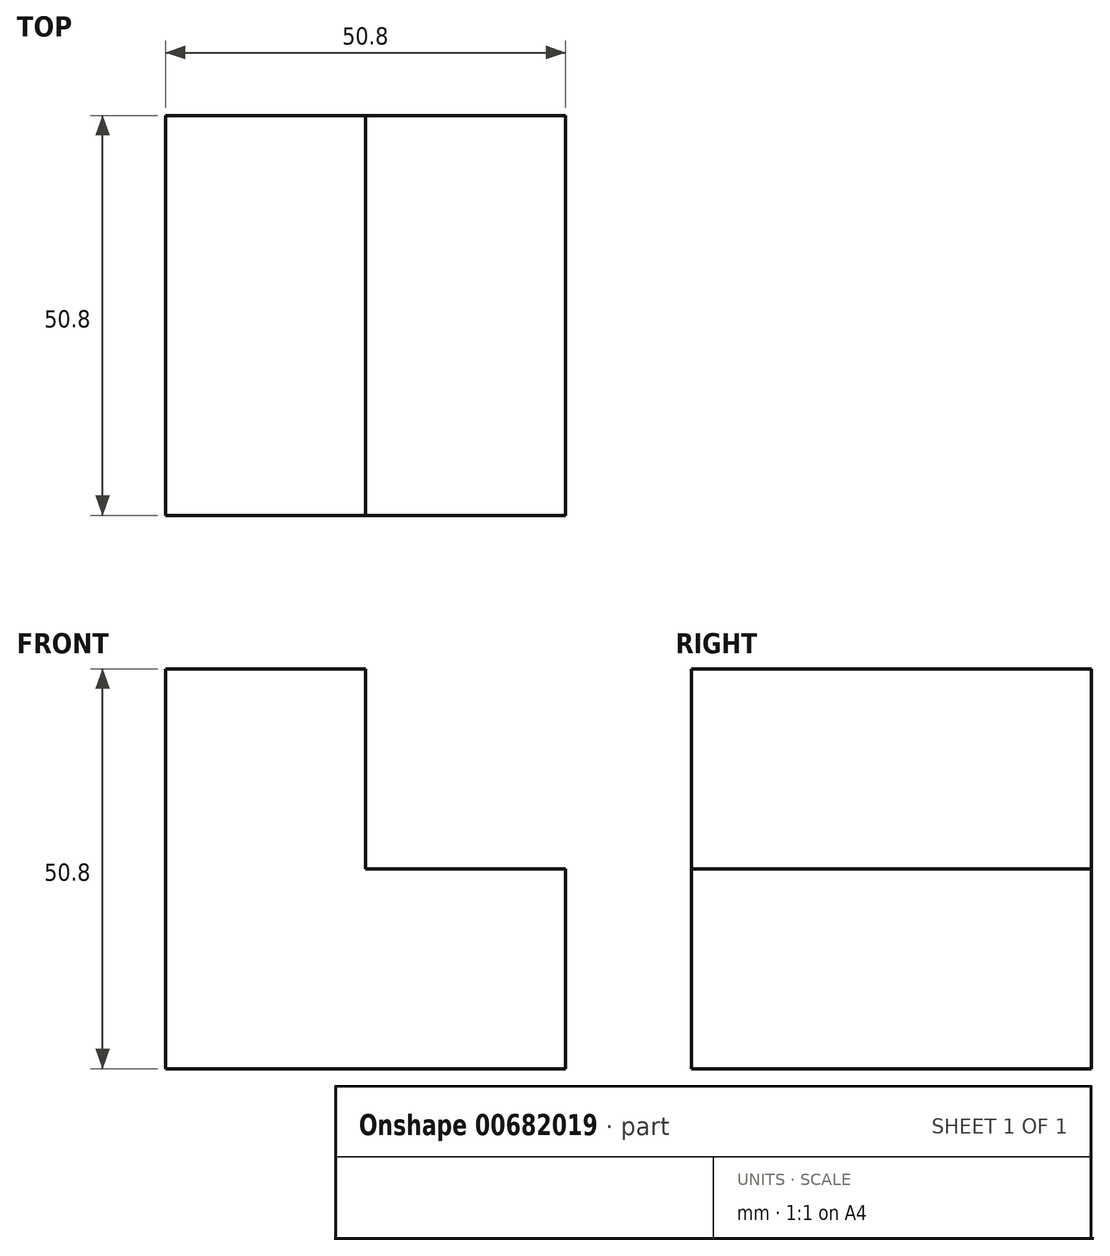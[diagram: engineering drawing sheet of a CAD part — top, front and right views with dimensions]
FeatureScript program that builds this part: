
annotation { "Feature Type Name" : "Feature", "Feature Type Description" : "" }
export const myFeature = defineFeature(function(context is Context, id is Id, definition is map)
    precondition{}
    {
        {
            var Q0;
            Q0=qCreatedBy(makeId("Front.planeOp"),FACE);
            var sketch = newSketch(context, id + "F0", { "sketchPlane" : qUnion([Q0])});
            skLineSegment(sketch, "E0", {"start": v(-51.9, 50.8) * mm, "end": v(-51.9, 0) * mm});
            skLineSegment(sketch, "E1", {"start": v(-51.9, 0) * mm, "end": v(-1.1, 0) * mm});
            skLineSegment(sketch, "E2", {"start": v(-1.1, 0) * mm, "end": v(-1.1, 25.4) * mm});
            skLineSegment(sketch, "E3", {"start": v(-1.1, 25.4) * mm, "end": v(-26.5, 25.4) * mm});
            skLineSegment(sketch, "E4", {"start": v(-26.5, 25.4) * mm, "end": v(-26.5, 50.8) * mm});
            skLineSegment(sketch, "E5", {"start": v(-26.5, 50.8) * mm, "end": v(-51.9, 50.8) * mm});
            skSolve(sketch);
        }
        {
            var Q0;
            Q0 = qSketchRegion(id + "F0", true);
            extrude(context, id + "F1", {"entities" : qUnion([Q0]), "depth" : 50.8 * mm, "offsetDistance" : 25.4 * mm});
        }
    });
